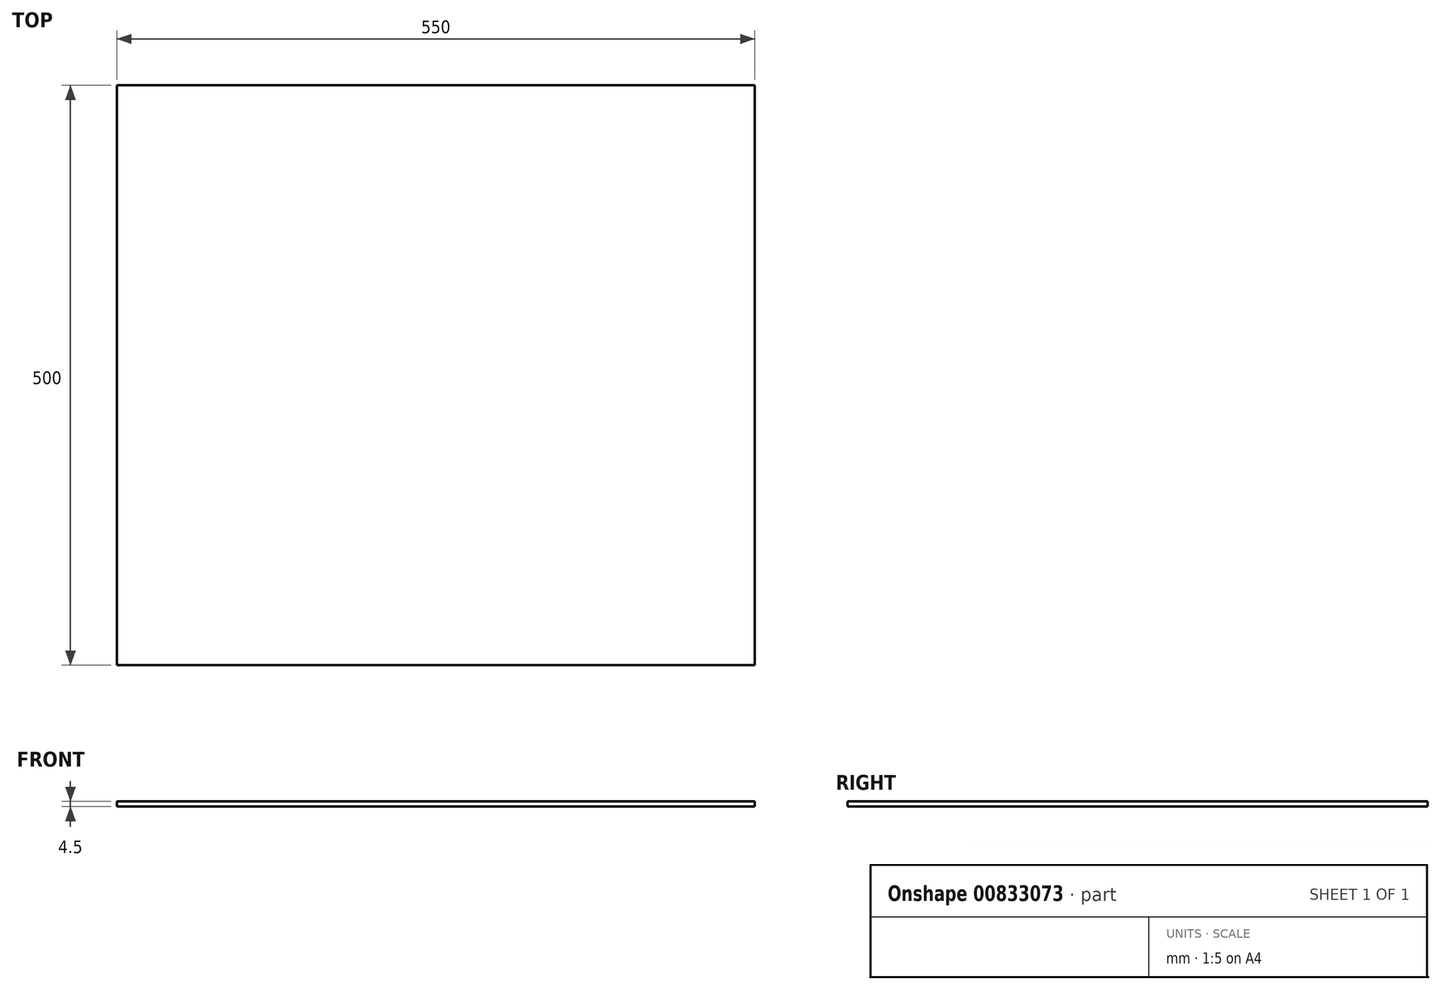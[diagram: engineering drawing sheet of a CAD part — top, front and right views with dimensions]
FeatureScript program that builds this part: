
annotation { "Feature Type Name" : "Feature", "Feature Type Description" : "" }
export const myFeature = defineFeature(function(context is Context, id is Id, definition is map)
    precondition{}
    {
        {
            var Q0;
            Q0=qCreatedBy(makeId("Top.planeOp"),FACE);
            var sketch = newSketch(context, id + "F0", { "sketchPlane" : qUnion([Q0])});
            skLineSegment(sketch, "E0.bottom", {"start": v(-254.47, 305.92) * mm, "end": v(295.53, 305.92) * mm});
            skLineSegment(sketch, "E0.top", {"start": v(-254.47, -194.08) * mm, "end": v(295.53, -194.08) * mm});
            skLineSegment(sketch, "E0.left", {"start": v(-254.47, 305.92) * mm, "end": v(-254.47, -194.08) * mm});
            skLineSegment(sketch, "E0.right", {"start": v(295.53, 305.92) * mm, "end": v(295.53, -194.08) * mm});
            skSolve(sketch);
        }
        {
            var Q0;
            Q0=makeQuery(id+"F0.imprint","IMPRINT",FACE,{"disambiguationData":[TD([[makeQuery(id+"F0.imprint","IMPRINT",EDGE,{"derivedFrom":sQuery(id+"F0.wireOp",EDGE,"E0.bottom")}),-1.0]])]});
            extrude(context, id + "F1", {"entities" : qUnion([Q0]), "depth" : 4 * mm, "offsetDistance" : 25 * mm});
        }
        {
            var Q0;
            Q0=makeQuery(id+"F1.opExtrude","CAP_FACE",FACE,{"disambiguationData":[OSD([sQuery(id+"F0.wireOp",EDGE,"E0.bottom"),sQuery(id+"F0.wireOp",EDGE,"E0.top"),sQuery(id+"F0.wireOp",EDGE,"E0.left"),sQuery(id+"F0.wireOp",EDGE,"E0.right")])],"isStart":false});
            extrude(context, id + "F2", {"entities" : qUnion([Q0]), "operationType" : NewBodyOperationType.ADD, "depth" : 0.5 * mm, "offsetDistance" : 25 * mm});
        }
        {
            var Q0;
            Q0=makeQuery(id+"F2.opExtrude","CAP_FACE",FACE,{"disambiguationData":[OSD([sQuery(id+"F0.wireOp",EDGE,"E0.bottom"),sQuery(id+"F0.wireOp",EDGE,"E0.top"),sQuery(id+"F0.wireOp",EDGE,"E0.left"),sQuery(id+"F0.wireOp",EDGE,"E0.right")])],"isStart":false});
            extrude(context, id + "F3", {"entities" : qUnion([Q0]), "operationType" : NewBodyOperationType.ADD, "depth" : .5 * mm, "offsetDistance" : 25 * mm});
        }
        {
            var Q0;
            Q0=makeQuery(id+"F3.opExtrude","CAP_FACE",FACE,{"disambiguationData":[OSD([sQuery(id+"F0.wireOp",EDGE,"E0.bottom"),sQuery(id+"F0.wireOp",EDGE,"E0.top"),sQuery(id+"F0.wireOp",EDGE,"E0.left"),sQuery(id+"F0.wireOp",EDGE,"E0.right")])],"isStart":false});
            extrude(context, id + "F4", {"entities" : qUnion([Q0]), "operationType" : NewBodyOperationType.REMOVE, "oppositeDirection" : true, "depth" : .5 * mm, "offsetDistance" : 25 * mm});
        }
    });
